# Revit family: IS_Softmood_Multiproduct_BIM_GB_T7831;T7832;T7837;T7838
name_source: partatom
category: Plumbing Fixtures
revit_build: Autodesk Revit MEP 2014 (Build: 20130308_1515(x64)
units: mm (PartAtom-declared; Revit-internal decimal feet)

## types (4) — shared parameters
Accessories = www.idealspec.co.uk
AreaUnits = millimeters
Assembly Code = C1030200
AssetType = Fixed
BREEAM = No
Brand = Ideal Standard
Color = Neutral / No Finish
ConnectionType = Plumbing
DurationUnit = year
ECA = No
ExpectedLife = 30
Finish = Neutral / No Finish
IfcExportAs = IfcFurnitureType
IfcExportType = Bathroom integrated duct work
InstallationInstructions = www.idealspec.co.uk/resources.html
LinearUnits = millimeters
Manufacturer = Ideal Standard (UK) Ltd
ManufacturerURL = www.idealspec.co.uk
MetalMtl = ISI_IdealStandard_Funiture_Chrome_Render
NBSDescription = Bathroom integrated duct work
NBSReference = 45-35-72/320
NominalDepth = 415 mm
NominalHeight = 109 mm
NominalLength = 415 mm
Shape = Rectangular
Space = Internal
SpareParts = www.fastpart-spares.co.uk
TMV3 = No
URL = www.idealspec.co.uk
Uniclass2015Code = Pr_40_30_78_06
Uniclass2015Title = Bathroom Shelves
Uniclass2015Version = Products v1.1
Version = 1
VolumeUnits = Litres
WRAS = No
WarrantyDescription = Manufacturers Warranty
WarrantyDurationParts = 5
WarrantyDurationUnit = year
WaterEfficientProduct = No
zero-valued in all types: Cost, Default Elevation

## per-type parameters (varying)
| type | BIMObjectName | BarCode | Description | Features | Model | ModelNumber | ModelReference | Name | NettWeight | NominalWidth | ProductInformation | Size |
| T783867 - Softmood 800 mm Bracket Set | ISI_IdealStandard_Furniture_Softmood_T783867 | 8014140385363 | Softmood bracket Set 80cm - for shelf solution | bracket Set 80cm - for shelf solution | T783867 | T783867 | Softmood bracket Set 80cm - for shelf solution | Furniture_Softmood_T783867_IdealStandard | 0.6 Kg | 730 mm  [stored 2.39501 ft] | www.idealspec.co.uk/assets/datasheet/T783867 | 109 x 416 x 730 mm |
| T783767 - Softmood 1000 mm Bracket Set | ISI_IdealStandard_Furniture_Softmood_T783767 | 8014140385356 | Softmood bracket Set 100cm - for shelf solution | bracket Set 100cm - for shelf solution | T783767 | T783767 | Softmood bracket Set 100cm - for shelf solution | Furniture_Softmood_T783767_IdealStandard | 0.7 Kg | 930 mm  [stored 3.05118 ft] | www.idealspec.co.uk/assets/datasheet/T783767 | 109 x 416 x 930 mm |
| T783267 - Softmood 1300 mm Bracket Set | ISI_IdealStandard_Furniture_Softmood_T783267 | 8014140385349 | Softmood bracket set 130cm - for shelf solution | bracket set 130cm - for shelf solution | T783267 | T783267 | Softmood bracket set 130cm - for shelf solution | Furniture_Softmood_T783267_IdealStandard | 3.7 Kg | 1230 mm  [stored 4.03543 ft] | www.idealspec.co.uk/assets/datasheet/T783267 | 109 x 416 x 1230 mm |
| T783167 - Softmood 600 mm Bracket set | ISI_IdealStandard_Furniture_Softmood_T783167 | 8014140385332 | Softmood bracket set 60cm - for shelf solution | bracket set 60cm - for shelf solution | T783167 | T783167 | Softmood bracket set 60cm - for shelf solution | Furniture_Softmood_T783167_IdealStandard | 2.1 Kg | 530 mm  [stored 1.73885 ft] | www.idealspec.co.uk/assets/datasheet/T783167 | 109 x 416 x 530 mm |

note: [stored X ft] marks values corroborated as IEEE doubles in the binary element streams (Revit-internal decimal feet)

## geometry (parser evidence)
native form markers: Sweep x1
no freeform markers — native parametric forms only
